# Revit family: Bath-Freestanding-KOHLER-EVOK-K-25167T_1
name_source: partatom
category: Plumbing Fixtures
units: mm (PartAtom-declared; Revit-internal decimal feet)

## family parameters
Cut with Voids When Loaded = No
Host = Face
Maintain Annotation Orientation = No
OmniClass Number = 23.31.15.00
OmniClass Title = Bathtubs
Part Type = Normal
Room Calculation Point = No
Round Connector Dimension = Use Diameter
Shared = No

## types (3) — shared parameters
ADA Compliant = No
Assembly Code = D2010500
CW Connection = No
Cold Water Inlet = Cold Water Inlet
Date Modified = 04/08/2022
Default Elevation = 0"
Drain Included = Yes
Finish = KOHLER-Acrylic-0-White
Flow Rate = 0 GPM
HW Connection = No
Height = 24 3/16"
Hot Water Inlet = Hot Water Inlet
Length = 29 1/2"
Manufacturer = Kohler Co.
Master Format 2014 = 22 41 19
Master Format 2014 Name = Residential Bathtubs
Material = Acrylic
Pressure = 0.00 psi
Product Documentation Link = https://files.kohler.com.cn
Product Name = EVOK
Product Page URL = https://www.kohler.com.cn
URL = http://www.kohler.com.cn
Vent Connection = No
Waste Connection = Yes
Waste Water Outlet = Waste Water Outlet
WaterSense Certified = No
Width = 59"

## per-type parameters (varying)
| type | Description | Model | Secondary Finish | Type |
| White Apron, 0-White | Ave 2.0 Oval 1.5m Seamless Freestanding Acrylic Bathtub (with Drain) | K-25167T-0 | KOHLER-Acrylic-0-White | 1 |
| Black Apron, 0-White | Ave 2.0 Oval 1.5m Seamless Freestanding Acrylic Bathtub Black Skirt (with Drain) | K-25167T-P5-0 | KOHLER-Acrylic-P5-Iron_Black | 2 |
| Peacock Apron, 0-White | Ave 2.0 Oval 1.5m Seamless Freestanding Acrylic Bathtub Peacock Blue Skirt (with Drainage) | K-25167T-P8-0 | KOHLER-Acrylic-P8-Peacock | 3 |

## geometry (parser evidence)
native form markers: Sweep x6
no freeform markers — native parametric forms only
